# Revit family: Shower-Showerhead-KOHLER-Geometric-K-45429ME_1
name_source: partatom
category: Plumbing Fixtures
units: mm (PartAtom-declared; Revit-internal decimal feet)

## family parameters
Cut with Voids When Loaded = No
Host = Face
OmniClass Number = 23.31.17.00
OmniClass Title = Showers
Part Type = Normal
Room Calculation Point = No
Round Connector Dimension = Use Diameter
Shared = No

## types (2) — shared parameters
ADA Compliant = No
Assembly Code = D2010700
CW Connection = No
Cold Water Inlet = Cold Water Inlet
Date Modified = 03/24/2023
Default Elevation = 72"
Description = Single-Function Showerhead
Drain Included = No
Flow Rate = 3 GPM
HW Connection = Yes
Height = 5 15/16"
Hot Water Inlet = Hot Water Inlet
Length = 6 13/16"
Manufacturer = Kohler Co.
Master Format 2014 = 22 42 23
Master Format 2014 Name = Residential Showers
Material = Premium Metal Construction
Panel Thickness = 0"
Pressure = 60.00 psi
Product Documentation Link = https://me.kohler.com
Product Name = Geometric
Product Page URL = https://me.kohler.com
Tempered Water inlet = Tempered Water inlet
URL = https://me.kohler.com
Vent Connection = No
Waste Connection = No
Waste Water Outlet = Waste Water Outlet
WaterSense Certified = No
Width = 4"

## per-type parameters (varying)
| type | Finish | Model | Type |
| CP-Polished Chrome | Kohler-Metal-CP-Polished_Chrome | K-45429ME-CP | 2 |
| AF-Vibrant French Gold | Kohler-Metal-AF-Vibrant_French_Gold | K-45429ME-AF | 1 |

## geometry (parser evidence)
native form markers: Sweep x6
no freeform markers — native parametric forms only
